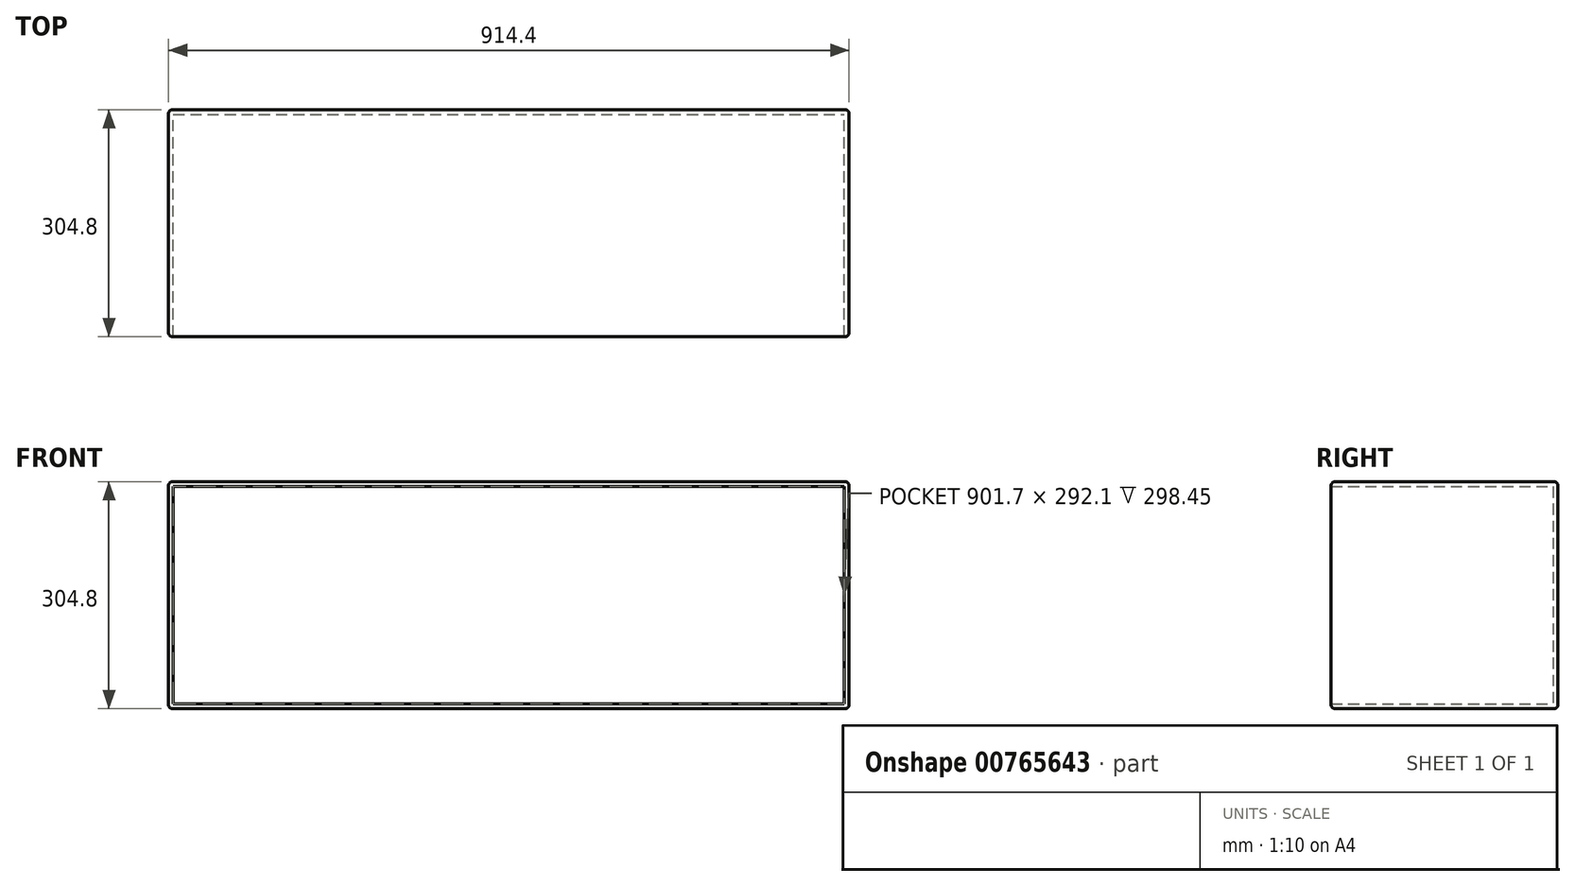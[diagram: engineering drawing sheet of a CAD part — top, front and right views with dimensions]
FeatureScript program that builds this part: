
annotation { "Feature Type Name" : "Feature", "Feature Type Description" : "" }
export const myFeature = defineFeature(function(context is Context, id is Id, definition is map)
    precondition{}
    {
        {
            var Q0;
            Q0=qCreatedBy(makeId("Front.planeOp"),FACE);
            var sketch = newSketch(context, id + "F0", { "sketchPlane" : qUnion([Q0])});
            skLineSegment(sketch, "E0.bottom", {"start": v(-462.18, -4.44) * mm, "end": v(452.22, -4.44) * mm});
            skLineSegment(sketch, "E0.top", {"start": v(-462.18, -309.24) * mm, "end": v(452.22, -309.24) * mm});
            skLineSegment(sketch, "E0.left", {"start": v(-462.18, -4.44) * mm, "end": v(-462.18, -309.24) * mm});
            skLineSegment(sketch, "E0.right", {"start": v(452.22, -4.44) * mm, "end": v(452.22, -309.24) * mm});
            skSolve(sketch);
        }
        {
            var Q0;
            Q0 = qSketchRegion(id + "F0", true);
            extrude(context, id + "F1", {"entities" : qUnion([Q0]), "depth" : 304.8 * mm, "offsetDistance" : 25.4 * mm});
        }
        {
            var Q0;
            Q0=makeQuery(id+"F1.opExtrude","CAP_FACE",FACE,{"disambiguationData":[OSD([sQuery(id+"F0.wireOp",EDGE,"E0.bottom"),sQuery(id+"F0.wireOp",EDGE,"E0.top"),sQuery(id+"F0.wireOp",EDGE,"E0.left"),sQuery(id+"F0.wireOp",EDGE,"E0.right")])],"isStart":false});
            shell(context, id + "F2", {"entities" : qUnion([Q0]), "thickness" : 6.35 * mm});
        }
        {
            var Q0;
            Q0=makeQuery(id+"F1.opExtrude","CAP_EDGE",EDGE,{"disambiguationData":[OSD([sQuery(id+"F0.wireOp",EDGE,"E0.bottom")])],"isStart":false});
            var Q1;
            Q1=makeQuery(id+"F1.opExtrude","CAP_EDGE",EDGE,{"disambiguationData":[OSD([sQuery(id+"F0.wireOp",EDGE,"E0.left")])],"isStart":false});
            var Q2;
            Q2=makeQuery(id+"F1.opExtrude","CAP_EDGE",EDGE,{"disambiguationData":[OSD([sQuery(id+"F0.wireOp",EDGE,"E0.top")])],"isStart":false});
            var Q3;
            Q3=makeQuery(id+"F1.opExtrude","CAP_EDGE",EDGE,{"disambiguationData":[OSD([sQuery(id+"F0.wireOp",EDGE,"E0.right")])],"isStart":false});
            fillet(context, id + "F3", {"entities" : qUnion([Q0, Q1, Q2, Q3]), "radius" : 5.08 * mm, "tangentPropagation" : true, "allowEdgeOverflow" : false});
        }
        {
            var Q0;
            Q0=makeQuery(id+"F1.opExtrude","SWEPT_FACE",FACE,{"disambiguationData":[OSD([sQuery(id+"F0.wireOp",EDGE,"E0.bottom")])]});
            var Q1;
            Q1=makeQuery(id+"F1.opExtrude","SWEPT_FACE",FACE,{"disambiguationData":[OSD([sQuery(id+"F0.wireOp",EDGE,"E0.left")])]});
            var Q2;
            Q2=makeQuery(id+"F1.opExtrude","SWEPT_FACE",FACE,{"disambiguationData":[OSD([sQuery(id+"F0.wireOp",EDGE,"E0.top")])]});
            var Q3;
            Q3=makeQuery(id+"F1.opExtrude","SWEPT_FACE",FACE,{"disambiguationData":[OSD([sQuery(id+"F0.wireOp",EDGE,"E0.right")])]});
            fillet(context, id + "F4", {"entities" : qUnion([Q0, Q1, Q2, Q3]), "radius" : 5.08 * mm, "tangentPropagation" : true, "allowEdgeOverflow" : false});
        }
    });
